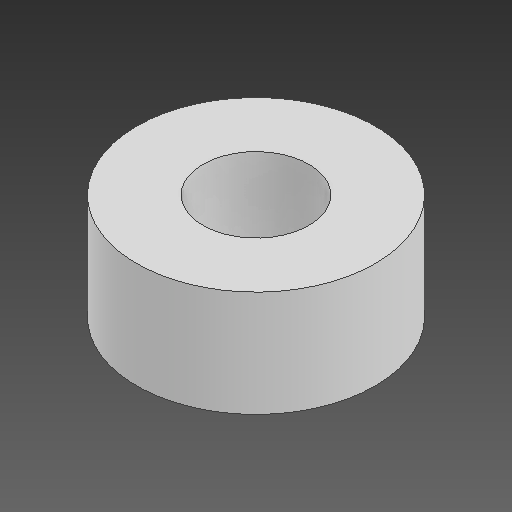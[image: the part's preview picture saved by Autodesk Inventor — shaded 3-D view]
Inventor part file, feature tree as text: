
AUTODESK INVENTOR PART (.ipt)
format: ipt  version: 2021 (Build 250183000, 183)  size: 99,840 bytes
history: native  units: in
note: dims shown in document units (in); Inventor stores cm internally (conversion verified against a paired STEP export)
features: other x3, sketch x1
ambient origin geometry x8: Origin, YZ Plane, XZ Plane, XY Plane, X Axis, Y Axis, Z Axis, Center Point
bodies: Solid1 (feature_tree)
feature tree (4):
  other  "bearing494.ipt"
  other  "Solid1::bearing494.ipt"
  other  "TaggingFeature1"
  sketch  "Sketch1"  dims[d0=0.3937in]
